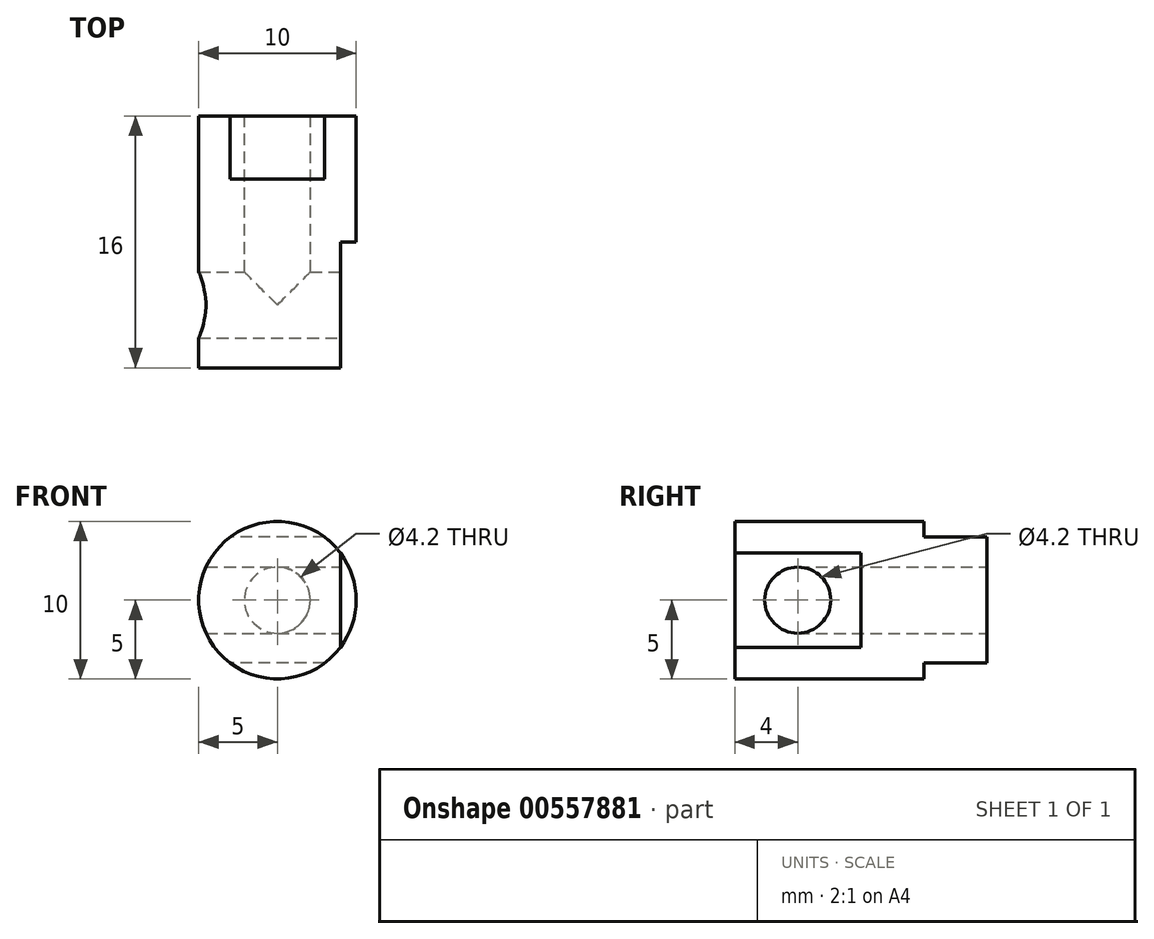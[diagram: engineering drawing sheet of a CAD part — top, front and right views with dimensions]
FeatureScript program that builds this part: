
annotation { "Feature Type Name" : "Feature", "Feature Type Description" : "" }
export const myFeature = defineFeature(function(context is Context, id is Id, definition is map)
    precondition{}
    {
        {
            var Q0;
            Q0=qCreatedBy(makeId("Front.planeOp"),FACE);
            var sketch = newSketch(context, id + "F0", { "sketchPlane" : qUnion([Q0])});
            skCircle(sketch, "E0", {"center": v(0, 0) * mm, "radius": 5 * mm});
            skSolve(sketch);
        }
        {
            var Q0;
            Q0 = qSketchRegion(id + "F0", true);
            var Q1;
            Q1 = qSketchRegion(id + "F2", true);
            extrude(context, id + "F1", {"entities" : qUnion([Q0, Q1]), "depth" : 16 * mm, "offsetDistance" : 25 * mm});
        }
        {
            var Q0;
            Q0=qCreatedBy(makeId("Right.planeOp"),FACE);
            var sketch = newSketch(context, id + "F2", { "sketchPlane" : qUnion([Q0])});
            skLineSegment(sketch, "E1.bottom", {"start": v(-4, 8.63) * mm, "end": v(0, 8.63) * mm});
            skLineSegment(sketch, "E1.top", {"start": v(-4, 4) * mm, "end": v(0, 4) * mm});
            skLineSegment(sketch, "E1.left", {"start": v(-4, 8.63) * mm, "end": v(-4, 4) * mm});
            skLineSegment(sketch, "E1.right", {"start": v(0, 8.63) * mm, "end": v(0, 4) * mm});
            skLineSegment(sketch, "E2.bottom", {"start": v(-4, -4) * mm, "end": v(7.27, -4) * mm});
            skLineSegment(sketch, "E2.top", {"start": v(-4, -13.13) * mm, "end": v(7.27, -13.13) * mm});
            skLineSegment(sketch, "E2.left", {"start": v(-4, -4) * mm, "end": v(-4, -13.13) * mm});
            skLineSegment(sketch, "E2.right", {"start": v(7.27, -4) * mm, "end": v(7.27, -13.13) * mm});
            skSolve(sketch);
        }
        {
            var Q0;
            Q0 = qSketchRegion(id + "F2", true);
            extrude(context, id + "F3", {"entities" : qUnion([Q0]), "operationType" : NewBodyOperationType.REMOVE, "endBound" : BoundingType.SYMMETRIC, "depth" : 25 * mm, "offsetDistance" : 25 * mm});
        }
        {
            var Q0;
            Q0=qCreatedBy(makeId("Top.planeOp"),FACE);
            var sketch = newSketch(context, id + "F4", { "sketchPlane" : qUnion([Q0])});
            skLineSegment(sketch, "E3.bottom", {"start": v(11.71, -22.83) * mm, "end": v(4, -22.83) * mm});
            skLineSegment(sketch, "E3.top", {"start": v(11.71, -8) * mm, "end": v(4, -8) * mm});
            skLineSegment(sketch, "E3.left", {"start": v(11.71, -22.83) * mm, "end": v(11.71, -8) * mm});
            skLineSegment(sketch, "E3.right", {"start": v(4, -22.83) * mm, "end": v(4, -8) * mm});
            skSolve(sketch);
        }
        {
            var Q0;
            Q0 = qSketchRegion(id + "F4", true);
            extrude(context, id + "F5", {"entities" : qUnion([Q0]), "operationType" : NewBodyOperationType.REMOVE, "endBound" : BoundingType.SYMMETRIC, "oppositeDirection" : true, "depth" : 25 * mm, "offsetDistance" : 25 * mm});
        }
        {
            var Q0;
            Q0=qCreatedBy(makeId("Right.planeOp"),FACE);
            var sketch = newSketch(context, id + "F6", { "sketchPlane" : qUnion([Q0])});
            skCircle(sketch, "E4", {"center": v(-12, 0) * mm, "radius": 2.1 * mm});
            skSolve(sketch);
        }
        {
            var Q0;
            Q0 = qSketchRegion(id + "F6", true);
            extrude(context, id + "F7", {"entities" : qUnion([Q0]), "operationType" : NewBodyOperationType.REMOVE, "endBound" : BoundingType.SYMMETRIC, "oppositeDirection" : true, "depth" : 25 * mm, "offsetDistance" : 25 * mm});
        }
        {
            var Q0;
            Q0=qCreatedBy(makeId("Front.planeOp"),FACE);
            var sketch = newSketch(context, id + "F8", { "sketchPlane" : qUnion([Q0])});
            skCircle(sketch, "E5", {"center": v(0, 0) * mm, "radius": 2.1 * mm});
            skSolve(sketch);
        }
        {
            var Q0;
            Q0 = qSketchRegion(id + "F8", true);
            extrude(context, id + "F9", {"entities" : qUnion([Q0]), "operationType" : NewBodyOperationType.REMOVE, "depth" : 12 * mm, "offsetDistance" : 25 * mm});
        }
    });
